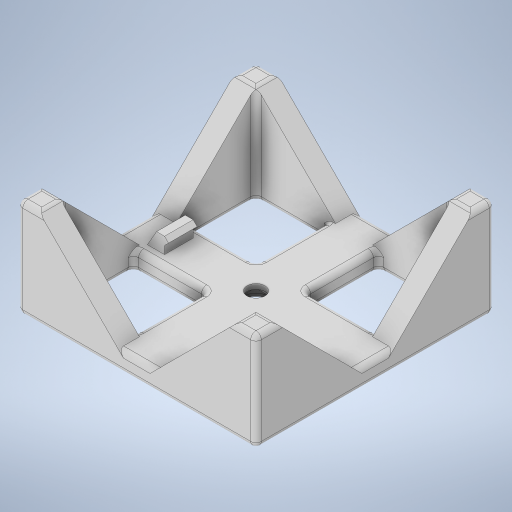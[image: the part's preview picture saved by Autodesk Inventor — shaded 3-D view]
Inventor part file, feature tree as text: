
AUTODESK INVENTOR PART (.ipt)
format: ipt  version: 2024 (Build 280153000, 153)  size: 598,016 bytes
history: native  units: in
note: dims shown in document units (in); Inventor stores cm internally (conversion verified against a paired STEP export)
features: extrude x9, fillet x4, chamfer x2, sketch x2, direct_edit x1, move_body x1
ambient origin geometry x8: Origin, YZ Plane, XZ Plane, XY Plane, X Axis, Y Axis, Z Axis, Center Point
bodies: Solid1 (feature_tree)
feature tree (19):
  extrude  "Extrusion2"  Depth=2.2146in
  extrude  "Extrusion3"  Depth=0.0787in
  extrude  "Extrusion4"  Depth=0.0787in
  extrude  "Extrusion5"  Depth=0.0787in
  extrude  "Extrusion6"  Depth=0.0787in
  extrude  "Extrusion8"  Depth=0.0787in
  extrude  "Extrusion9"  Depth=0.0787in
  extrude  "Extrusion11"  Depth=0.0787in
  extrude  "Extrusion12"  Depth=0.0787in TaperAngle=0.0deg
  chamfer  "Chamfer2"  Distance=0.315in
  chamfer  "Chamfer3"  Distance=0.315in
  direct_edit  "Direct Edit1"
  fillet  "Fillet1"  Radius=0.315in
  fillet  "Fillet3"  Radius=0.315in
  fillet  "Fillet4"  Radius=0.315in
  fillet  "Fillet5"  Radius=0.315in
  sketch  "Sketch3"  dims[d3=0.4862in d4=0.2657in d11=2.2146in d12=2.2146in]
  sketch  "Sketch4"  dims[d13=1.2587in d14=1.2786in d15=1.2786in d16=0.1181in d17=0.1181in d18=0.1181in d19=0.1181in d20=0.3543in d23=0.2205in d24=0.0in d25=0.315in d26=0.315in d27=0.315in d28=0.315in d29=0.315in d30=0.315in d31=0.315in d32=0.315in d33=1.1811in d34=0.0in d35=0.0354in d36=0.0in d37=0.0236in d38=0.0in d39=0.0118in d40=0.0in d41=3.5433in d42=3.5433in d48=0.3543in d49=45.0deg d50=0.1181in d51=0.0in d52=0.0in d55=45.0deg d56=0.1181in d57=0.0in d58=0.0in d61=0.0157in d62=0.0157in d63=0.0157in d64=0.0157in d65=1.1467in d66=0.2126in d67=0.1181in d68=0.2362in d69=0.0in d70=0.0591in d71=0.0in d72=0.0591in d73=0.0787in d74=45.0deg d75=0.2362in d76=0.0787in d77=30.0deg d78=0.0in d79=0.0in d80=0.063in d84=0.0787in d86=0.0787in d87=0.0787in d88=0.0787in d85=0.0344in]
  move_body  "Move1"
